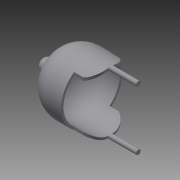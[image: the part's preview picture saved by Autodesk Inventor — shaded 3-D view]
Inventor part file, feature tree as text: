
AUTODESK INVENTOR PART (.ipt)
format: ipt  version: 2015 SP1 (Build 190203100, 203)  size: 208,896 bytes
history: native  units: in
note: dims shown in document units (in); Inventor stores cm internally (conversion verified against a paired STEP export)
features: sketch x3, extrude x2, revolve x1
ambient origin geometry x8: Origin, YZ Plane, XZ Plane, XY Plane, X Axis, Y Axis, Z Axis, Center Point
bodies: Solid1 (feature_tree)
feature tree (6):
  revolve  "Revolution1"  [1 undecoded]
  extrude  "Extrusion1"  Depth=0.25in
  extrude  "Extrusion2"  TaperAngle=90.0deg  [1 undecoded]
  sketch  "Sketch1"  dims[d0=0.5in d4=6.0in]
  sketch  "Sketch3"  dims[d5=3.05in d6=0.25in]
  sketch  "Sketch4"  dims[d7=0.5in d8=90.0deg d9=1.5in d14=1.0in d15=1.0in d18=1.3688in d22=2.0954in d23=1.4126in d24=1.0in d25=0.0in d26=0.75in d27=0.05in d28=0.5in d30=3.2001in d31=0.5in d32=3.2in d33=3.0in d34=0.0in]
note: 2 required parameter values undecoded (feature->parameter linkage not recoverable at this tier; creation-order binding heuristic only, values carry confidence <= 0.55)